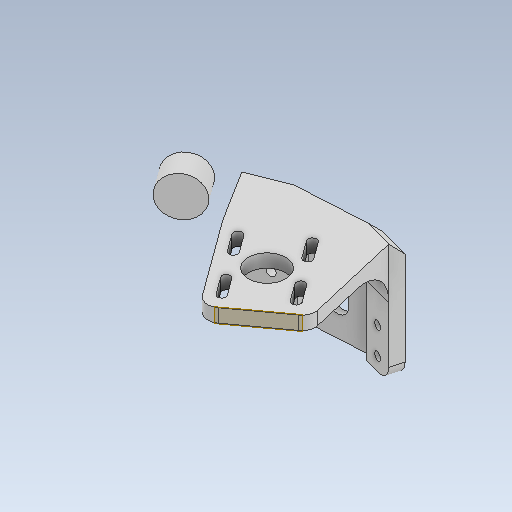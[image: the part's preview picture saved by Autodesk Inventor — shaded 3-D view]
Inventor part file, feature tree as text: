
AUTODESK INVENTOR PART (.ipt)
format: ipt  version: 2020 (Build 240168000, 168)  size: 335,872 bytes
history: native  units: mm
features: reference x10, other x8, sketch x7, extrude x5, fillet x4, projected_geometry x4, plane x2, hole x2, thicken_offset x1, chamfer x1, shell x1
ambient origin geometry x8: Origin, YZ Plane, XZ Plane, XY Plane, X Axis, Y Axis, Z Axis, Center Point
bodies: Solid1 (feature_tree)
feature tree (45):
  plane  "Work Plane1"
  extrude  "Extrusion1"  Depth=5.0mm
  extrude  "Extrusion2"  Depth=5.0mm
  thicken_offset  "Thicken1"
  hole  "Hole1"  [1 undecoded]
  hole  "Hole2"  [1 undecoded]
  extrude  "Extrusion3"  Depth=8.0mm
  fillet  "Fillet1"  Radius=20.0mm
  fillet  "Fillet2"  Radius=20.0mm
  chamfer  "Chamfer1"  Distance=40.0mm
  fillet  "Fillet3"  Radius=4.0mm
  fillet  "Fillet4"  Radius=3.0mm
  extrude  "Extrusion4"  Depth=4.0mm
  plane  "Work Plane2"
  extrude  "Extrusion5"  Depth=10.0mm
  sketch  "Sketch1"  dims[d0=5.0mm d1=5.0mm]
  reference  "Reference1"
  reference  "Reference2"
  reference  "Reference3"
  reference  "Reference4"
  sketch  "Sketch2"  dims[d2=5.0mm d3=5.0mm]
  projected_geometry  "Projected Loop1"
  projected_geometry  "Projected Loop2"
  sketch  "Sketch3"  dims[d4=25.0mm d5=0.0mm d6=25.0mm d7=0.0mm]
  reference  "Reference5"
  reference  "Reference6"
  sketch  "Sketch4"  dims[d8=20.0mm d9=20.0mm]
  reference  "Reference7"
  reference  "Reference8"
  sketch  "Sketch5"  dims[d10=3.0mm d11=6.0mm d12=4.0mm d13=2.0mm d14=90.0deg d15=8.0mm d16=20.594885mm]
  reference  "Reference9"
  projected_geometry  "Projected Loop3"
  sketch  "Sketch6"  dims[d17=3.0mm d18=6.0mm d19=4.0mm d20=2.0mm d21=90.0deg d22=8.0mm d23=20.594885mm d24=102.0mm d25=20.0mm d26=20.0mm]
  projected_geometry  "Projected Loop4"
  sketch  "Sketch7"  dims[d27=30.0mm d28=40.0mm d29=4.0mm d30=3.0mm d31=4.0mm d32=3.2mm d33=4.0mm d34=3.2mm d35=4.0mm d36=3.2mm d37=14.0mm d38=5.0mm d39=0.0mm d40=14.0mm d41=2.0mm d42=5.0mm d43=2.0mm d44=45.0deg d45=5.0mm d46=5.0mm d47=18.0mm d48=6.0mm d49=8.0mm d50=5.0mm d51=0.0mm d52=0.0mm d53=55.0mm d54=15.0mm d55=10.0mm d56=0.0mm]
  reference  "Reference10"
  parser-record x2  (decoder bookkeeping rows leaked as tree rows — omitted from the tree; the rows remain in map.json)
  other  "reducer_2.iam"
  other  "motor_h_1:1"
  shell  "shell_2:1"  Thickness=4.0mm
  other  "t_base_linker_2:1"
  other  "leg_1.iam"
  other  "reducer_2:1"
  other  "bearing_8_16_5:1"
note: 2 required parameter values undecoded (feature->parameter linkage not recoverable at this tier; creation-order binding heuristic only, values carry confidence <= 0.55)
note: 2 file-system paths scrubbed to <path> (originals preserved in map.json)
